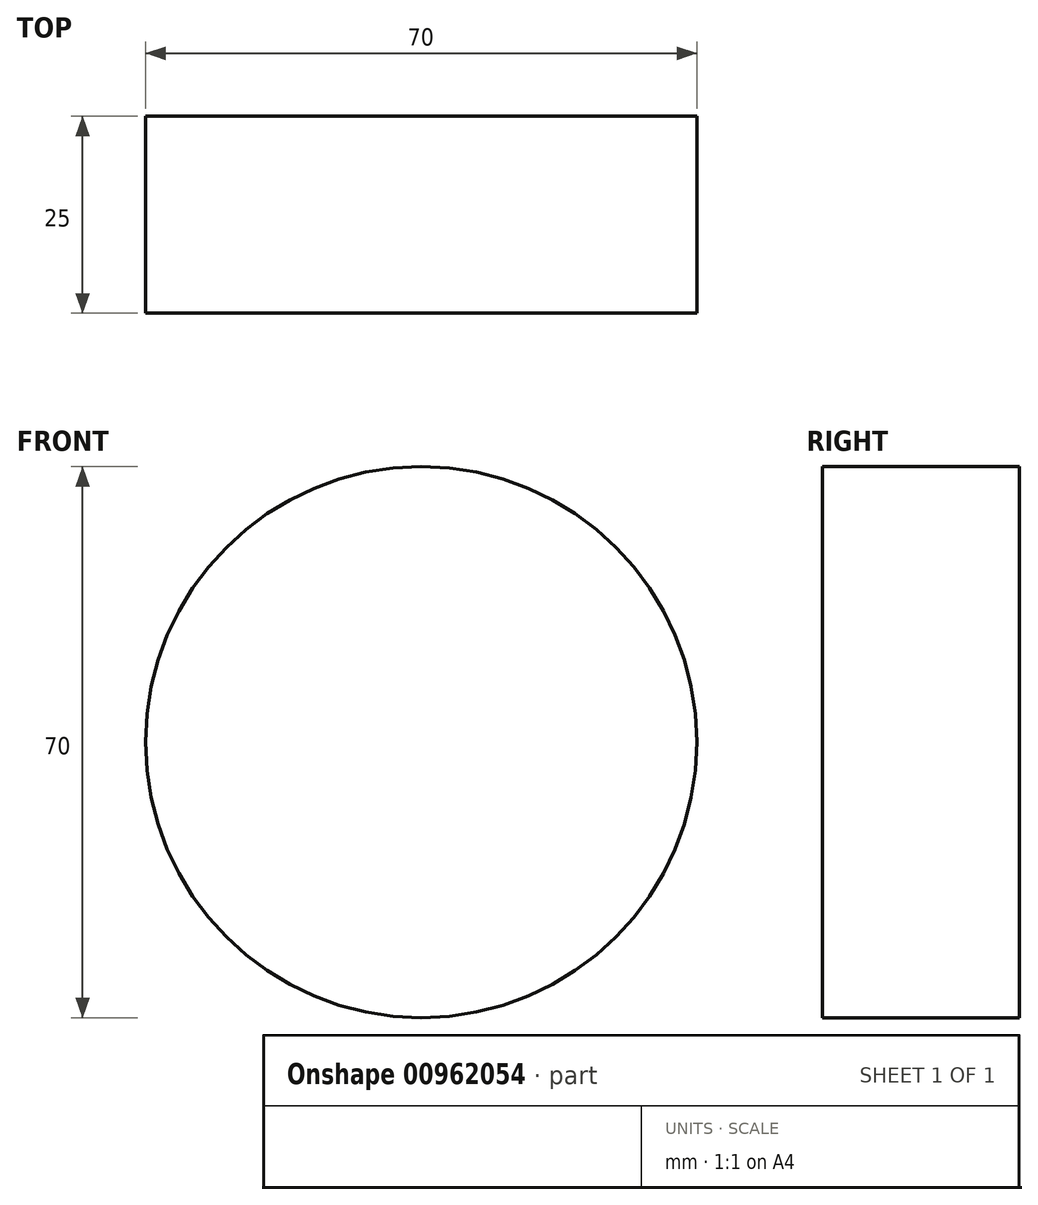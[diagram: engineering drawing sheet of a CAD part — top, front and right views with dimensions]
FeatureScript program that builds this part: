
annotation { "Feature Type Name" : "Feature", "Feature Type Description" : "" }
export const myFeature = defineFeature(function(context is Context, id is Id, definition is map)
    precondition{}
    {
        {
            var Q0;
            Q0=qCreatedBy(makeId("Front.planeOp"),FACE);
            var sketch = newSketch(context, id + "F0", { "sketchPlane" : qUnion([Q0])});
            skCircle(sketch, "E0", {"center": v(0, 0) * mm, "radius": 35 * mm});
            skSolve(sketch);
        }
        {
            var Q0;
            Q0=makeQuery(id+"F0.imprint","IMPRINT",FACE,{"disambiguationData":[TD([[makeQuery(id+"F0.imprint","IMPRINT",EDGE,{"derivedFrom":sQuery(id+"F0.wireOp",EDGE,"E0")}),1.0]])]});
            extrude(context, id + "F1", {"entities" : qUnion([Q0]), "depth" : 25 * mm, "offsetDistance" : 25 * mm});
        }
    });
